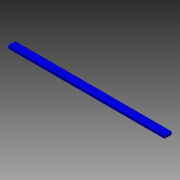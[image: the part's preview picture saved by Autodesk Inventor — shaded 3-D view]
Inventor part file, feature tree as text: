
AUTODESK INVENTOR PART (.ipt)
format: ipt  version: 2012 (Build 160160000, 160)  size: 76,288 bytes
history: native  units: mm
features: extrude x1, sketch x1
ambient origin geometry x8: Origin, YZ Plane, XZ Plane, XY Plane, X Axis, Y Axis, Z Axis, Center Point
bodies: Solid1 (feature_tree)
feature tree (2):
  extrude  "Extrusion1"  Depth=206.0mm
  sketch  "Sketch1"  dims[d0=10.0mm d1=206.0mm d2=1.0mm d3=3.0mm d4=0.0mm d5=1.0mm]
